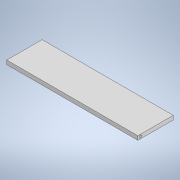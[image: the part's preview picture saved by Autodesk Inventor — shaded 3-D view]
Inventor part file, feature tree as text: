
AUTODESK INVENTOR PART (.ipt)
format: ipt  version: 2020.3 (Build 243373000, 373)  size: 100,864 bytes
history: native  units: mm
features: extrude x2, sketch x2
ambient origin geometry x8: Origin, YZ Plane, XZ Plane, XY Plane, X Axis, Y Axis, Z Axis, Center Point
bodies: Solid1 (feature_tree)
feature tree (4):
  extrude  "Extrusion1"  Depth=35.0mm
  extrude  "Extrusion2"  Depth=4.0mm
  sketch  "Sketch1"  dims[d0=130.0mm d1=35.0mm]
  sketch  "Sketch2"  dims[d2=4.0mm d3=0.0mm d4=2.5mm d5=2.5mm d6=0.0mm d7=0.0mm]
